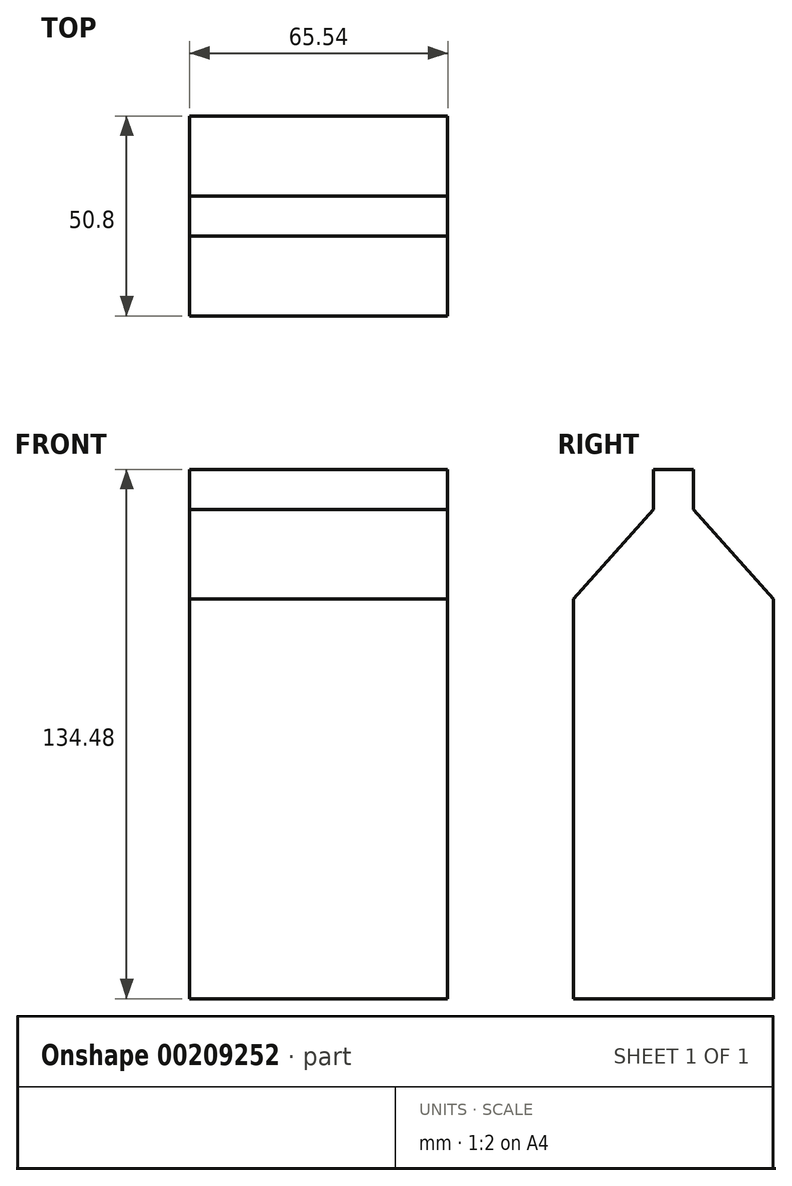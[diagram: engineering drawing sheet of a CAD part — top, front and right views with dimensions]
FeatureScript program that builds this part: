
annotation { "Feature Type Name" : "Feature", "Feature Type Description" : "" }
export const myFeature = defineFeature(function(context is Context, id is Id, definition is map)
    precondition{}
    {
        {
            var Q0;
            Q0=qCreatedBy(makeId("Right.planeOp"),FACE);
            var sketch = newSketch(context, id + "F0", { "sketchPlane" : qUnion([Q0])});
            skLineSegment(sketch, "E0.bottom", {"start": v(25.4, -83.96) * mm, "end": v(-25.4, -83.96) * mm});
            skLineSegment(sketch, "E0.left", {"start": v(25.4, -83.96) * mm, "end": v(25.4, 17.64) * mm});
            skLineSegment(sketch, "E0.right", {"start": v(-25.4, -83.96) * mm, "end": v(-25.4, 17.64) * mm});
            skPoint(sketch, "E0.middle", {"position": v(0, -33.16) * mm});
            skLineSegment(sketch, "E1", {"start": v(25.4, 17.64) * mm, "end": v(5.08, 40.36) * mm});
            skLineSegment(sketch, "E2", {"start": v(5.08, 50.52) * mm, "end": v(5.08, 40.36) * mm});
            skLineSegment(sketch, "E3", {"start": v(5.08, 50.52) * mm, "end": v(0, 50.52) * mm});
            skLineSegment(sketch, "E4.MirrorCS", {"start": v(-5.08, 50.52) * mm, "end": v(0, 50.52) * mm});
            skLineSegment(sketch, "E5.MirrorCS", {"start": v(-5.08, 50.52) * mm, "end": v(-5.08, 40.36) * mm});
            skLineSegment(sketch, "E6.MirrorCS", {"start": v(-25.4, 17.64) * mm, "end": v(-5.08, 40.36) * mm});
            skSolve(sketch);
        }
        {
            var Q0;
            Q0=makeQuery(id+"F0.imprint","IMPRINT",FACE,{"disambiguationData":[TD([[makeQuery(id+"F0.imprint","IMPRINT",EDGE,{"derivedFrom":sQuery(id+"F0.wireOp",EDGE,"E0.bottom")}),-1.0]])]});
            extrude(context, id + "F1", {"entities" : qUnion([Q0]), "endBound" : BoundingType.SYMMETRIC, "oppositeDirection" : true, "depth" : 65.53 * mm});
        }
    });
